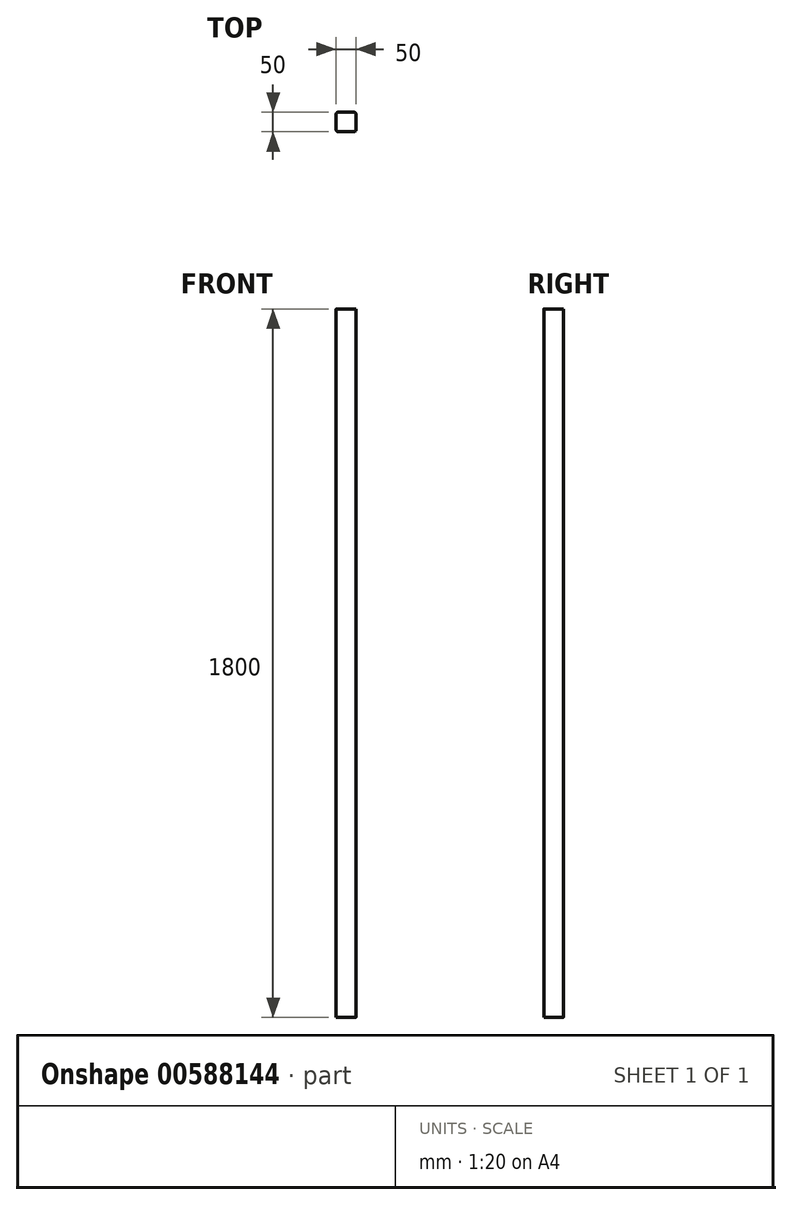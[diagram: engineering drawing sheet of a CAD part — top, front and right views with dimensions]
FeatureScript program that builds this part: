
annotation { "Feature Type Name" : "Feature", "Feature Type Description" : "" }
export const myFeature = defineFeature(function(context is Context, id is Id, definition is map)
    precondition{}
    {
        {
            var Q0;
            Q0=qCreatedBy(makeId("Front.planeOp"),FACE);
            var sketch = newSketch(context, id + "F0", { "sketchPlane" : qUnion([Q0])});
            skLineSegment(sketch, "E0.bottom", {"start": v(-24.23, 1315.7) * mm, "end": v(25.77, 1315.7) * mm});
            skLineSegment(sketch, "E0.top", {"start": v(-24.23, -484.3) * mm, "end": v(25.77, -484.3) * mm});
            skLineSegment(sketch, "E0.left", {"start": v(-24.23, 1315.7) * mm, "end": v(-24.23, -484.3) * mm});
            skLineSegment(sketch, "E0.right", {"start": v(25.77, 1315.7) * mm, "end": v(25.77, -484.3) * mm});
            skSolve(sketch);
        }
        {
            var Q0;
            Q0 = qSketchRegion(id + "F0", true);
            extrude(context, id + "F1", {"entities" : qUnion([Q0]), "endBound" : BoundingType.SYMMETRIC, "depth" : 50 * mm, "offsetDistance" : 25 * mm});
        }
        {
            var Q0;
            Q0=makeQuery(id+"F1.opExtrude","CAP_EDGE",EDGE,{"disambiguationData":[OSD([sQuery(id+"F0.wireOp",EDGE,"E0.right")])],"isStart":false});
            var Q1;
            Q1=makeQuery(id+"F1.opExtrude","CAP_EDGE",EDGE,{"disambiguationData":[OSD([sQuery(id+"F0.wireOp",EDGE,"E0.left")])],"isStart":false});
            var Q2;
            Q2=makeQuery(id+"F1.opExtrude","CAP_EDGE",EDGE,{"disambiguationData":[OSD([sQuery(id+"F0.wireOp",EDGE,"E0.left")])],"isStart":true});
            var Q3;
            Q3=makeQuery(id+"F1.opExtrude","CAP_EDGE",EDGE,{"disambiguationData":[OSD([sQuery(id+"F0.wireOp",EDGE,"E0.right")])],"isStart":true});
            fillet(context, id + "F2", {"entities" : qUnion([Q0, Q1, Q2, Q3]), "radius" : 5 * mm, "tangentPropagation" : true, "allowEdgeOverflow" : false});
        }
    });
